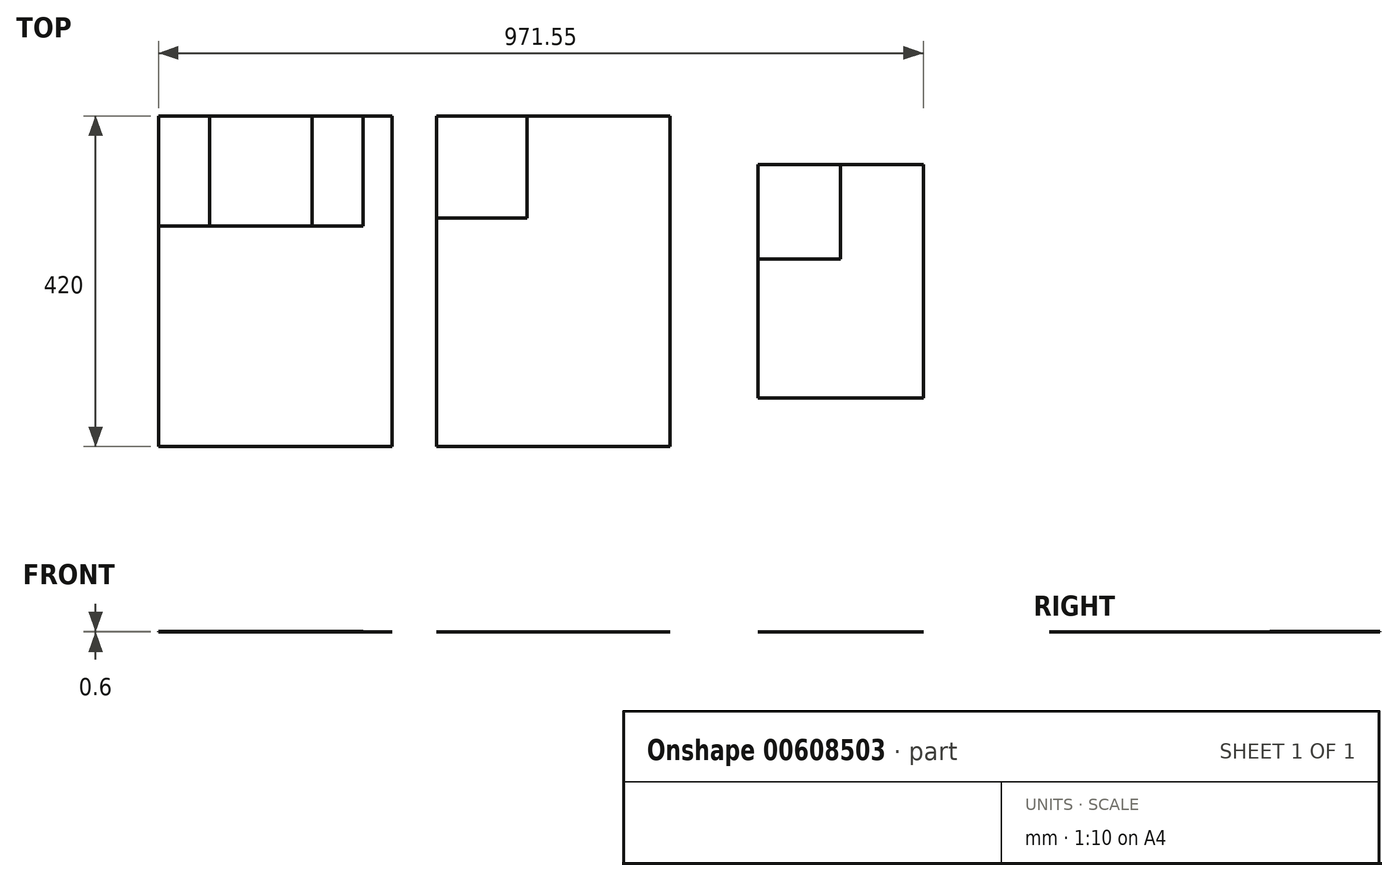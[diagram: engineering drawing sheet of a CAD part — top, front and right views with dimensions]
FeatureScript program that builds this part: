
annotation { "Feature Type Name" : "Feature", "Feature Type Description" : "" }
export const myFeature = defineFeature(function(context is Context, id is Id, definition is map)
    precondition{}
    {
        {
            var Q0;
            Q0=qCreatedBy(makeId("Top.planeOp"),FACE);
            var sketch = newSketch(context, id + "F0", { "sketchPlane" : qUnion([Q0])});
            skLineSegment(sketch, "E0.bottom", {"start": v(148.5, -210) * mm, "end": v(-148.5, -210) * mm});
            skLineSegment(sketch, "E0.top", {"start": v(148.5, 210) * mm, "end": v(-148.5, 210) * mm});
            skLineSegment(sketch, "E0.left", {"start": v(148.5, -210) * mm, "end": v(148.5, 210) * mm});
            skLineSegment(sketch, "E0.right", {"start": v(-148.5, -210) * mm, "end": v(-148.5, 210) * mm});
            skPoint(sketch, "E0.middle", {"position": v(0, 0) * mm});
            skLineSegment(sketch, "E1.bottom", {"start": v(501.48, -210) * mm, "end": v(204.48, -210) * mm});
            skLineSegment(sketch, "E1.top", {"start": v(501.48, 210) * mm, "end": v(204.48, 210) * mm});
            skLineSegment(sketch, "E1.left", {"start": v(501.48, -210) * mm, "end": v(501.48, 210) * mm});
            skLineSegment(sketch, "E1.right", {"start": v(204.48, -210) * mm, "end": v(204.48, 210) * mm});
            skPoint(sketch, "E1.middle", {"position": v(352.98, 0) * mm});
            skLineSegment(sketch, "E2.bottom", {"start": v(823.05, -148.5) * mm, "end": v(613.05, -148.5) * mm});
            skLineSegment(sketch, "E2.top", {"start": v(823.05, 148.5) * mm, "end": v(613.05, 148.5) * mm});
            skLineSegment(sketch, "E2.left", {"start": v(823.05, -148.5) * mm, "end": v(823.05, 148.5) * mm});
            skLineSegment(sketch, "E2.right", {"start": v(613.05, -148.5) * mm, "end": v(613.05, 148.5) * mm});
            skPoint(sketch, "E2.middle", {"position": v(718.05, 0) * mm});
            skSolve(sketch);
        }
        {
            var Q0;
            Q0=makeQuery(id+"F0.imprint","IMPRINT",FACE,{"disambiguationData":[TD([[makeQuery(id+"F0.imprint","IMPRINT",EDGE,{"derivedFrom":sQuery(id+"F0.wireOp",EDGE,"E0.bottom")}),-1.0]])]});
            var Q1;
            Q1=makeQuery(id+"F0.imprint","IMPRINT",FACE,{"disambiguationData":[TD([[makeQuery(id+"F0.imprint","IMPRINT",EDGE,{"derivedFrom":sQuery(id+"F0.wireOp",EDGE,"E1.bottom")}),-1.0]])]});
            var Q2;
            Q2=makeQuery(id+"F0.imprint","IMPRINT",FACE,{"disambiguationData":[TD([[makeQuery(id+"F0.imprint","IMPRINT",EDGE,{"derivedFrom":sQuery(id+"F0.wireOp",EDGE,"E2.bottom")}),-1.0]])]});
            extrude(context, id + "F1", {"entities" : qUnion([Q0, Q1, Q2]), "depth" : .1 * mm, "offsetDistance" : 25 * mm});
        }
        {
            var Q0;
            Q0=makeQuery(id+"F1.opExtrude","CAP_FACE",FACE,{"disambiguationData":[OSD([sQuery(id+"F0.wireOp",EDGE,"E1.bottom"),sQuery(id+"F0.wireOp",EDGE,"E1.top"),sQuery(id+"F0.wireOp",EDGE,"E1.left"),sQuery(id+"F0.wireOp",EDGE,"E1.right")])],"isStart":false});
            var sketch = newSketch(context, id + "F2", { "sketchPlane" : qUnion([Q0])});
            skLineSegment(sketch, "E3.bottom", {"start": v(-148.5, 210) * mm, "end": v(111.5, 210) * mm});
            skLineSegment(sketch, "E3.top", {"start": v(-148.5, 70) * mm, "end": v(111.5, 70) * mm});
            skLineSegment(sketch, "E3.left", {"start": v(-148.5, 210) * mm, "end": v(-148.5, 70) * mm});
            skLineSegment(sketch, "E3.right", {"start": v(111.5, 210) * mm, "end": v(111.5, 70) * mm});
            skLineSegment(sketch, "E4.top", {"start": v(-148.5, -70) * mm, "end": v(111.5, -70) * mm});
            skLineSegment(sketch, "E4.left", {"start": v(-148.5, 70) * mm, "end": v(-148.5, -70) * mm});
            skLineSegment(sketch, "E4.right", {"start": v(111.5, 70) * mm, "end": v(111.5, -70) * mm});
            skLineSegment(sketch, "E5.top", {"start": v(-148.5, -210) * mm, "end": v(111.5, -210) * mm});
            skLineSegment(sketch, "E5.left", {"start": v(-148.5, -70) * mm, "end": v(-148.5, -210) * mm});
            skLineSegment(sketch, "E5.right", {"start": v(111.5, -70) * mm, "end": v(111.5, -210) * mm});
            skLineSegment(sketch, "E6.bottom", {"start": v(204.48, 210) * mm, "end": v(319.48, 210) * mm});
            skLineSegment(sketch, "E6.left", {"start": v(204.48, 210) * mm, "end": v(204.48, 80) * mm});
            skLineSegment(sketch, "E7", {"start": v(204.48, 80) * mm, "end": v(319.48, 80) * mm});
            skLineSegment(sketch, "E8", {"start": v(319.48, 80) * mm, "end": v(319.48, 210) * mm});
            skLineSegment(sketch, "E9.0.1.0", {"start": v(319.48, -50) * mm, "end": v(319.48, 80) * mm});
            skLineSegment(sketch, "E9.0.1.1", {"start": v(204.48, -50) * mm, "end": v(319.48, -50) * mm});
            skLineSegment(sketch, "E9.0.1.3", {"start": v(204.48, 80) * mm, "end": v(204.48, -50) * mm});
            skLineSegment(sketch, "E9.0.2.0", {"start": v(319.48, -180) * mm, "end": v(319.48, -50) * mm});
            skLineSegment(sketch, "E9.0.2.1", {"start": v(204.48, -180) * mm, "end": v(319.48, -180) * mm});
            skLineSegment(sketch, "E9.0.2.2", {"start": v(204.48, -50) * mm, "end": v(319.48, -50) * mm});
            skLineSegment(sketch, "E9.0.2.3", {"start": v(204.48, -50) * mm, "end": v(204.48, -180) * mm});
            skLineSegment(sketch, "E9.1.0.0", {"start": v(434.38, 80) * mm, "end": v(434.38, 210) * mm});
            skLineSegment(sketch, "E9.1.0.1", {"start": v(319.38, 80) * mm, "end": v(434.38, 80) * mm});
            skLineSegment(sketch, "E9.1.0.2", {"start": v(319.38, 210) * mm, "end": v(434.38, 210) * mm});
            skLineSegment(sketch, "E9.1.0.3", {"start": v(319.38, 210) * mm, "end": v(319.38, 80) * mm});
            skLineSegment(sketch, "E9.1.1.0", {"start": v(434.38, -50) * mm, "end": v(434.38, 80) * mm});
            skLineSegment(sketch, "E9.1.1.1", {"start": v(319.38, -50) * mm, "end": v(434.38, -50) * mm});
            skLineSegment(sketch, "E9.1.1.2", {"start": v(319.38, 80) * mm, "end": v(434.38, 80) * mm});
            skLineSegment(sketch, "E9.1.1.3", {"start": v(319.38, 80) * mm, "end": v(319.38, -50) * mm});
            skLineSegment(sketch, "E9.1.2.0", {"start": v(434.38, -180) * mm, "end": v(434.38, -50) * mm});
            skLineSegment(sketch, "E9.1.2.1", {"start": v(319.38, -180) * mm, "end": v(434.38, -180) * mm});
            skLineSegment(sketch, "E9.1.2.2", {"start": v(319.38, -50) * mm, "end": v(434.38, -50) * mm});
            skLineSegment(sketch, "E9.1.2.3", {"start": v(319.38, -50) * mm, "end": v(319.38, -180) * mm});
            skLineSegment(sketch, "E9.direction1", {"start": v(204.48, 80) * mm, "end": v(319.38, 80) * mm, "construction": true});
            skLineSegment(sketch, "E9.direction2", {"start": v(204.48, 80) * mm, "end": v(204.48, -50) * mm, "construction": true});
            skSolve(sketch);
        }
        {
            var Q0;
            Q0=makeQuery(id+"F2.imprint","IMPRINT",FACE,{"disambiguationData":[TD([[makeQuery(id+"F2.imprint","IMPRINT",EDGE,{"derivedFrom":sQuery(id+"F2.wireOp",EDGE,"E3.bottom")}),-1.0]])]});
            extrude(context, id + "F3", {"entities" : qUnion([Q0]), "depth" : .1 * mm, "offsetDistance" : 25 * mm});
        }
        {
            var Q0;
            Q0=makeQuery(id+"F1.opExtrude","CAP_FACE",FACE,{"disambiguationData":[OSD([sQuery(id+"F0.wireOp",EDGE,"E2.bottom"),sQuery(id+"F0.wireOp",EDGE,"E2.top"),sQuery(id+"F0.wireOp",EDGE,"E2.left"),sQuery(id+"F0.wireOp",EDGE,"E2.right")])],"isStart":false});
            var sketch = newSketch(context, id + "F4", { "sketchPlane" : qUnion([Q0])});
            skLineSegment(sketch, "E10", {"start": v(-18.5, 210) * mm, "end": v(-18.5, 70) * mm, "construction": true});
            skLineSegment(sketch, "E11", {"start": v(-83.5, 210) * mm, "end": v(-83.5, 70) * mm});
            skLineSegment(sketch, "E12", {"start": v(46.5, 210) * mm, "end": v(46.5, 70) * mm});
            skLineSegment(sketch, "E13.bottom", {"start": v(-148.5, 210) * mm, "end": v(-83.5, 210) * mm});
            skLineSegment(sketch, "E13.top", {"start": v(-148.5, 70) * mm, "end": v(-83.5, 70) * mm});
            skLineSegment(sketch, "E13.left", {"start": v(-148.5, 210) * mm, "end": v(-148.5, 70) * mm});
            skLineSegment(sketch, "E14.bottom", {"start": v(-83.5, 70) * mm, "end": v(46.5, 70) * mm});
            skLineSegment(sketch, "E14.top", {"start": v(-83.5, 210) * mm, "end": v(46.5, 210) * mm});
            skLineSegment(sketch, "E14.left", {"start": v(-83.5, 70) * mm, "end": v(-83.5, 210) * mm});
            skLineSegment(sketch, "E14.right", {"start": v(46.5, 70) * mm, "end": v(46.5, 210) * mm});
            skLineSegment(sketch, "E15.bottom", {"start": v(46.5, 210) * mm, "end": v(111.5, 210) * mm});
            skLineSegment(sketch, "E15.top", {"start": v(46.5, 70) * mm, "end": v(111.5, 70) * mm});
            skLineSegment(sketch, "E15.right", {"start": v(111.5, 210) * mm, "end": v(111.5, 70) * mm});
            skLineSegment(sketch, "E16.bottom", {"start": v(613.05, 148.5) * mm, "end": v(718.05, 148.5) * mm});
            skLineSegment(sketch, "E16.top", {"start": v(613.05, 28.5) * mm, "end": v(718.05, 28.5) * mm});
            skLineSegment(sketch, "E16.left", {"start": v(613.05, 148.5) * mm, "end": v(613.05, 28.5) * mm});
            skLineSegment(sketch, "E16.right", {"start": v(718.05, 148.5) * mm, "end": v(718.05, 28.5) * mm});
            skLineSegment(sketch, "E17.0.1.8", {"start": v(613, 28.5) * mm, "end": v(718, 28.5) * mm});
            skLineSegment(sketch, "E18.0.1.0", {"start": v(718.05, 28.5) * mm, "end": v(718.05, -91.5) * mm});
            skLineSegment(sketch, "E18.0.1.1", {"start": v(613.05, 28.5) * mm, "end": v(613.05, -91.5) * mm});
            skLineSegment(sketch, "E18.0.1.3", {"start": v(613, -91.5) * mm, "end": v(718, -91.5) * mm});
            skLineSegment(sketch, "E18.0.1.4", {"start": v(613.05, -91.5) * mm, "end": v(718.05, -91.5) * mm});
            skLineSegment(sketch, "E18.1.0.0", {"start": v(823.05, 148.5) * mm, "end": v(823.05, 28.5) * mm});
            skLineSegment(sketch, "E18.1.0.2", {"start": v(718.05, 148.5) * mm, "end": v(823.05, 148.5) * mm});
            skLineSegment(sketch, "E18.1.0.3", {"start": v(718, 28.5) * mm, "end": v(823, 28.5) * mm});
            skLineSegment(sketch, "E18.1.0.4", {"start": v(718.05, 28.5) * mm, "end": v(823.05, 28.5) * mm});
            skLineSegment(sketch, "E18.1.1.0", {"start": v(823.05, 28.5) * mm, "end": v(823.05, -91.5) * mm});
            skLineSegment(sketch, "E18.1.1.1", {"start": v(718.05, 28.5) * mm, "end": v(718.05, -91.5) * mm});
            skLineSegment(sketch, "E18.1.1.2", {"start": v(718.05, 28.5) * mm, "end": v(823.05, 28.5) * mm});
            skLineSegment(sketch, "E18.1.1.3", {"start": v(718, -91.5) * mm, "end": v(823, -91.5) * mm});
            skLineSegment(sketch, "E18.1.1.4", {"start": v(718.05, -91.5) * mm, "end": v(823.05, -91.5) * mm});
            skLineSegment(sketch, "E18.direction1", {"start": v(613, 28.5) * mm, "end": v(718, 28.5) * mm, "construction": true});
            skLineSegment(sketch, "E18.direction2", {"start": v(613, 28.5) * mm, "end": v(613, -91.5) * mm, "construction": true});
            skSolve(sketch);
        }
        {
            var Q0;
            Q0=makeQuery(id+"F4.imprint","IMPRINT",FACE,{"disambiguationData":[TD([[makeQuery(id+"F4.imprint","IMPRINT",EDGE,{"derivedFrom":sQuery(id+"F4.wireOp",EDGE,"E13.bottom")}),-1.0]])]});
            extrude(context, id + "F5", {"entities" : qUnion([Q0]), "depth" : .5 * mm, "offsetDistance" : 25 * mm});
        }
        {
            var Q0;
            Q0=makeQuery(id+"F4.imprint","IMPRINT",FACE,{"disambiguationData":[TD([[makeQuery(id+"F4.imprint","IMPRINT",EDGE,{"derivedFrom":sQuery(id+"F4.wireOp",EDGE,"E14.bottom")}),1.0]])]});
            extrude(context, id + "F6", {"entities" : qUnion([Q0]), "depth" : .5 * mm, "offsetDistance" : 25 * mm});
        }
        {
            var Q0;
            Q0=makeQuery(id+"F4.imprint","IMPRINT",FACE,{"disambiguationData":[TD([[makeQuery(id+"F4.imprint","IMPRINT",EDGE,{"derivedFrom":sQuery(id+"F4.wireOp",EDGE,"E15.bottom")}),-1.0]])]});
            extrude(context, id + "F7", {"entities" : qUnion([Q0]), "depth" : .5 * mm, "offsetDistance" : 25 * mm});
        }
        {
            var Q0;
            Q0=makeQuery(id+"F2.imprint","IMPRINT",FACE,{"disambiguationData":[TD([[makeQuery(id+"F2.imprint","IMPRINT",EDGE,{"derivedFrom":sQuery(id+"F2.wireOp",EDGE,"E6.bottom")}),1.0]])]});
            extrude(context, id + "F8", {"entities" : qUnion([Q0]), "depth" : .1 * mm, "offsetDistance" : 25 * mm});
        }
        {
            var Q0;
            Q0=makeQuery(id+"F4.imprint","IMPRINT",FACE,{"disambiguationData":[TD([[makeQuery(id+"F4.imprint","IMPRINT",EDGE,{"derivedFrom":sQuery(id+"F4.wireOp",EDGE,"E16.bottom")}),1.0]])]});
            extrude(context, id + "F9", {"entities" : qUnion([Q0]), "depth" : .1 * mm, "offsetDistance" : 25 * mm});
        }
    });
